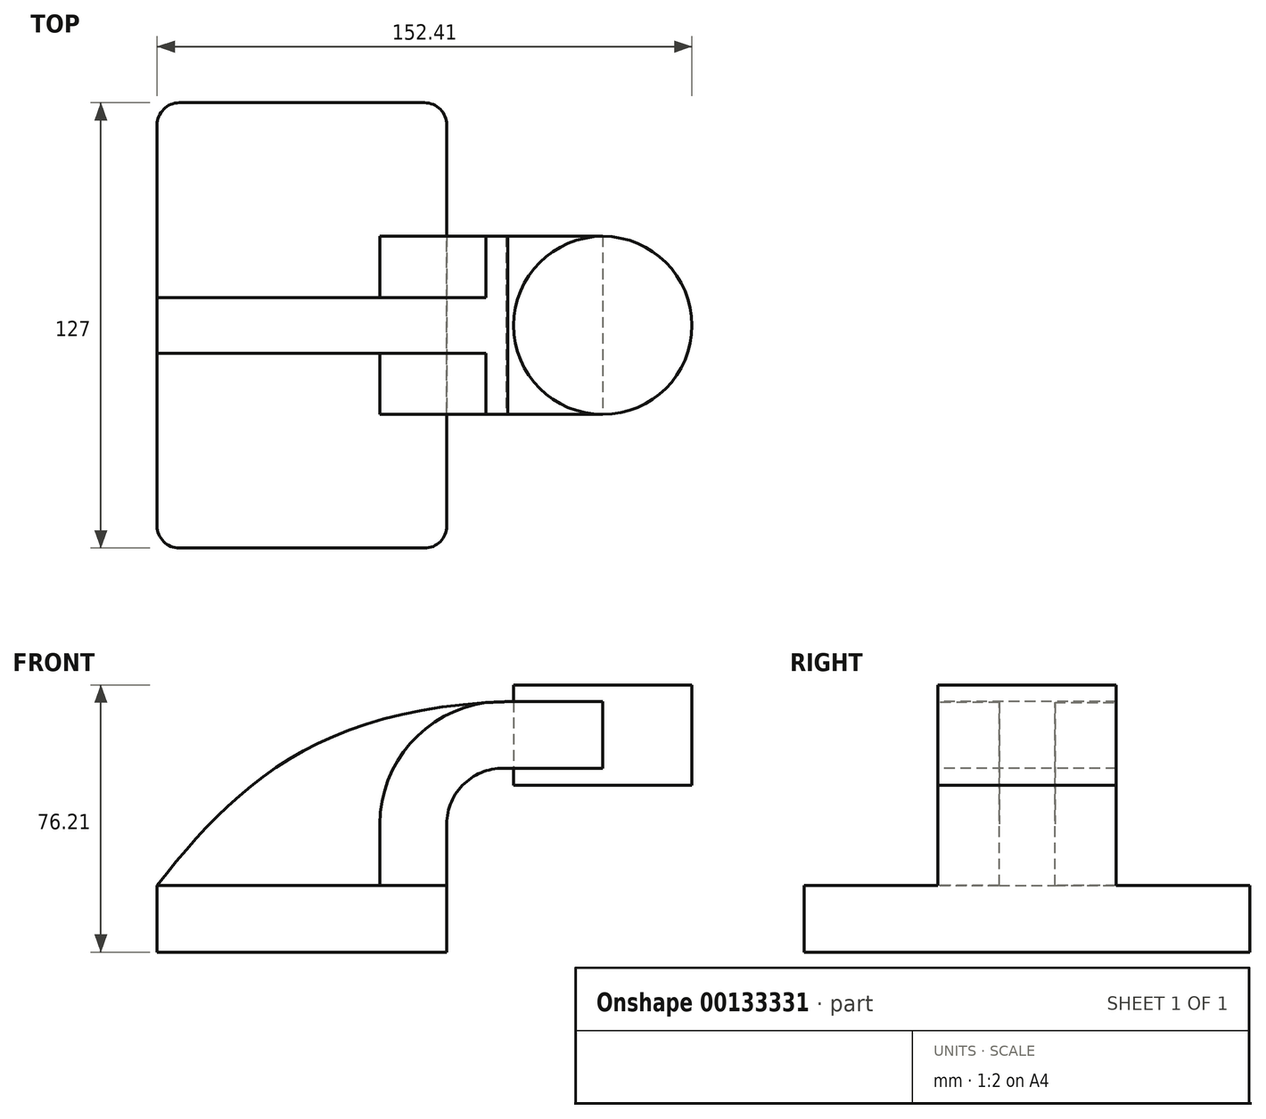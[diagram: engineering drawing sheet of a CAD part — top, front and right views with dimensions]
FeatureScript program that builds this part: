
annotation { "Feature Type Name" : "Feature", "Feature Type Description" : "" }
export const myFeature = defineFeature(function(context is Context, id is Id, definition is map)
    precondition{}
    {
        {
            var Q0;
            Q0=qCreatedBy(makeId("Front.planeOp"),FACE);
            var sketch = newSketch(context, id + "F0", { "sketchPlane" : qUnion([Q0])});
            skLineSegment(sketch, "E0.bottom", {"start": v(41.28, -9.52) * mm, "end": v(-41.28, -9.53) * mm});
            skLineSegment(sketch, "E0.top", {"start": v(41.28, 9.53) * mm, "end": v(-41.28, 9.53) * mm});
            skLineSegment(sketch, "E0.left", {"start": v(41.28, -9.52) * mm, "end": v(41.28, 9.53) * mm});
            skLineSegment(sketch, "E0.right", {"start": v(-41.28, -9.53) * mm, "end": v(-41.28, 9.53) * mm});
            skPoint(sketch, "E0.middle", {"position": v(0, 0) * mm});
            skLineSegment(sketch, "E1.bottom", {"start": v(60.32, 38.1) * mm, "end": v(111.12, 38.1) * mm});
            skLineSegment(sketch, "E1.top", {"start": v(60.32, 66.67) * mm, "end": v(111.12, 66.67) * mm});
            skLineSegment(sketch, "E1.left", {"start": v(60.33, 38.1) * mm, "end": v(60.32, 66.68) * mm});
            skLineSegment(sketch, "E1.right", {"start": v(111.12, 38.1) * mm, "end": v(111.12, 66.68) * mm});
            skPoint(sketch, "E1.middle", {"position": v(85.72, 52.39) * mm});
            skLineSegment(sketch, "E2", {"start": v(41.28, 9.53) * mm, "end": v(41.28, 27) * mm});
            skArc(sketch, "E3", {"start": v(41.27, 27) * mm, "mid": v(46.29, 38.57) * mm, "end": v(58.15, 42.84) * mm});
            skLineSegment(sketch, "E4", {"start": v(58.15, 42.84) * mm, "end": v(85.73, 42.84) * mm});
            skLineSegment(sketch, "E5.0", {"start": v(58.64, 61.9) * mm, "end": v(85.73, 61.9) * mm});
            skArc(sketch, "E5.1", {"start": v(22.23, 27) * mm, "mid": v(32.99, 52.22) * mm, "end": v(58.64, 61.9) * mm});
            skLineSegment(sketch, "E5.2", {"start": v(22.22, 9.53) * mm, "end": v(22.22, 27) * mm});
            skLineSegment(sketch, "E6", {"start": v(85.73, 42.84) * mm, "end": v(85.73, 61.9) * mm});
            skFitSpline(sketch, "E7", {"points": [v(-41.28, 9.52) * mm, v(58.64, 61.9) * mm], "startDerivative": vector(64.94, 82.54) * mm, "endDerivative": vector(164.41, 4.97) * mm});
            skLineSegment(sketch, "E8", {"start": v(85.72, 38.1) * mm, "end": v(85.72, 66.67) * mm});
            skSolve(sketch);
        }
        {
            var Q0;
            Q0=makeQuery(id+"F0.imprint","IMPRINT",FACE,{"disambiguationData":[TD([[makeQuery(id+"F0.imprint","IMPRINT",EDGE,{"derivedFrom":sQuery(id+"F0.wireOp",EDGE,"E0.bottom")}),-1.0]])]});
            extrude(context, id + "F1", {"entities" : qUnion([Q0]), "endBound" : BoundingType.SYMMETRIC, "depth" : 127 * mm});
        }
        {
            var Q0;
            {var subQ1=sQuery(id+"F0.wireOp",EDGE,"E2");Q0=makeQuery(id+"F0.imprint","IMPRINT",FACE,{"disambiguationData":[TD([[makeQuery(id+"F0.imprint","IMPRINT",EDGE,{"derivedFrom":subQ1}),1.0]])]});}
            var Q1;
            {var subQ5=sQuery(id+"F0.wireOp",EDGE,"E6");Q1=makeQuery(id+"F0.imprint","IMPRINT",FACE,{"disambiguationData":[TD([[makeQuery(id+"F0.imprint","IMPRINT",EDGE,{"derivedFrom":subQ5}),1.0]])]});}
            var Q2;
            {var subQ0=sQuery(id+"F0.wireOp",EDGE,"E4");var subQ1=sQuery(id+"F0.wireOp",EDGE,"E1.left");var subQ2=makeQuery(id+"F0.imprint","INTERSECT",VERTEX,{"derivedFrom":[subQ1,subQ0]});Q2=makeQuery(id+"F0.imprint","IMPRINT",FACE,{"disambiguationData":[TD([[makeQuery(id+"F0.imprint","IMPRINT",EDGE,{"disambiguationData":[TD([[subQ2,-1.0]])],"derivedFrom":subQ1}),-1.0]])]});}
            extrude(context, id + "F2", {"entities" : qUnion([Q0, Q1, Q2]), "operationType" : NewBodyOperationType.ADD, "endBound" : BoundingType.SYMMETRIC, "oppositeDirection" : true, "depth" : 50.8 * mm});
        }
        {
            var Q0;
            {var subQ3=sQuery(id+"F0.wireOp",EDGE,"E5.2");Q0=makeQuery(id+"F0.imprint","IMPRINT",FACE,{"disambiguationData":[TD([[makeQuery(id+"F0.imprint","IMPRINT",EDGE,{"derivedFrom":subQ3}),1.0]])]});}
            extrude(context, id + "F3", {"entities" : qUnion([Q0]), "operationType" : NewBodyOperationType.ADD, "endBound" : BoundingType.SYMMETRIC, "depth" : 15.88 * mm});
        }
        {
            var Q0;
            {var subQ0=sQuery(id+"F0.wireOp",EDGE,"E1.right");Q0=makeQuery(id+"F0.imprint","IMPRINT",FACE,{"disambiguationData":[TD([[makeQuery(id+"F0.imprint","IMPRINT",EDGE,{"derivedFrom":subQ0}),1.0]])]});}
            var Q1;
            Q1=sQuery(id+"F0.wireOp",EDGE,"E6");
            revolve(context, id + "F4", {"entities" : qUnion([Q0]), "axis" : qUnion([Q1]), "revolveType" : RevolveType.FULL});
        }
        {
            var Q0;
            Q0=makeQuery(id+"F1.opExtrude","CAP_EDGE",EDGE,{"disambiguationData":[OSD([sQuery(id+"F0.wireOp",EDGE,"E0.left")])],"isStart":true});
            var Q1;
            Q1=makeQuery(id+"F1.opExtrude","CAP_EDGE",EDGE,{"disambiguationData":[OSD([sQuery(id+"F0.wireOp",EDGE,"E0.left")])],"isStart":false});
            var Q2;
            Q2=makeQuery(id+"F1.opExtrude","CAP_EDGE",EDGE,{"disambiguationData":[OSD([sQuery(id+"F0.wireOp",EDGE,"E0.right")])],"isStart":false});
            var Q3;
            Q3=makeQuery(id+"F1.opExtrude","CAP_EDGE",EDGE,{"disambiguationData":[OSD([sQuery(id+"F0.wireOp",EDGE,"E0.right")])],"isStart":true});
            fillet(context, id + "F5", {"entities" : qUnion([Q0, Q1, Q2, Q3]), "radius" : 6.35 * mm, "tangentPropagation" : true, "allowEdgeOverflow" : false});
        }
    });
